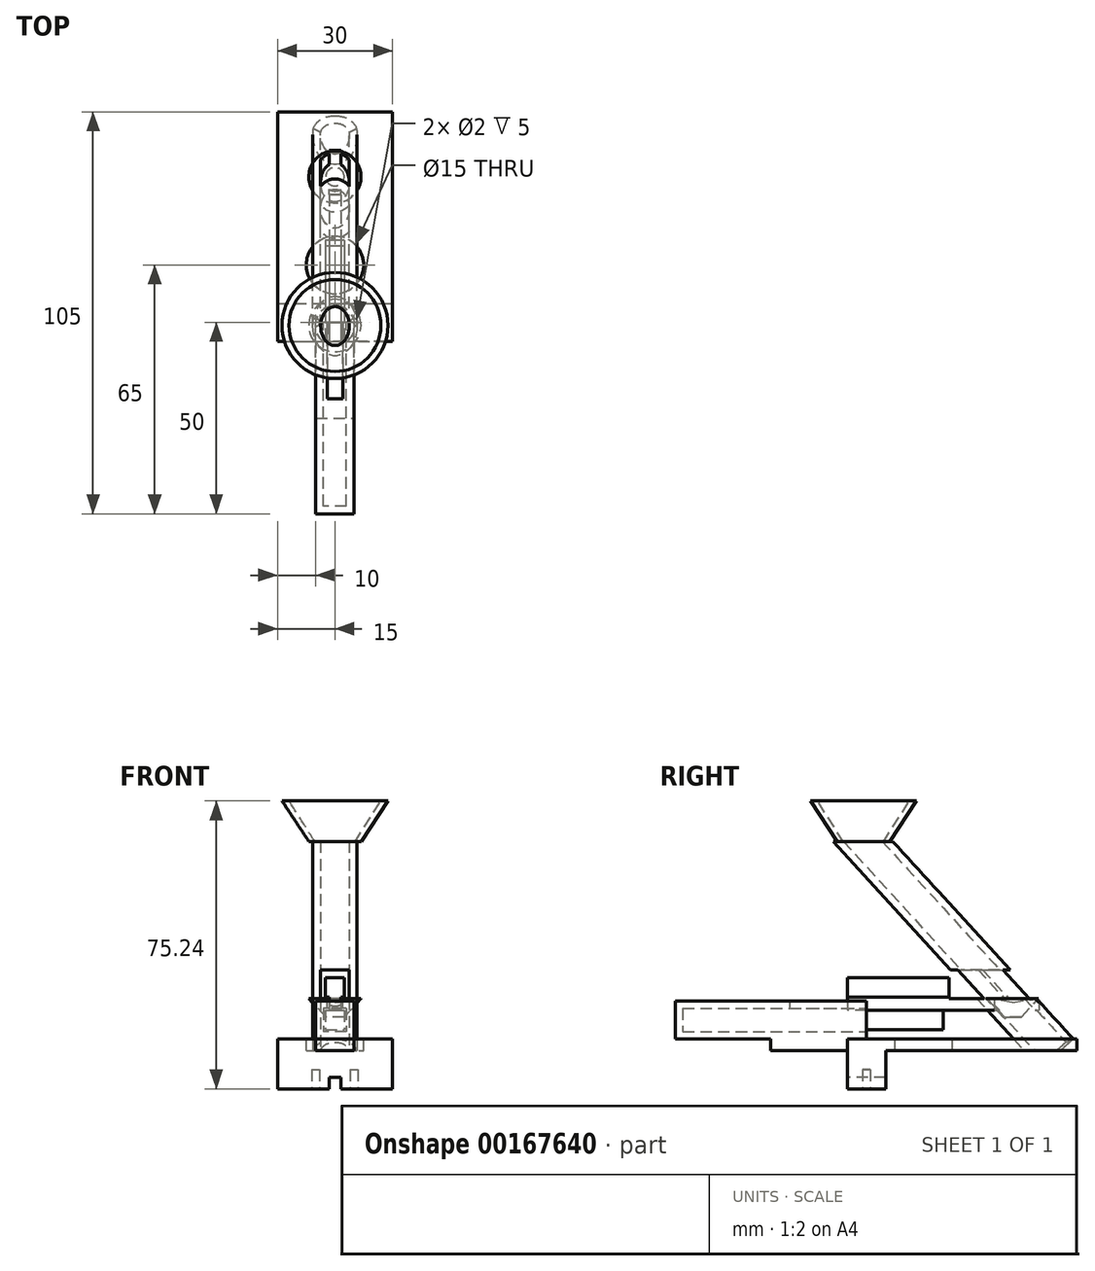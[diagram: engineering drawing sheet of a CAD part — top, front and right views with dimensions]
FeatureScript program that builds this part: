
annotation { "Feature Type Name" : "Feature", "Feature Type Description" : "" }
export const myFeature = defineFeature(function(context is Context, id is Id, definition is map)
    precondition{}
    {
        {
            var Q0;
            Q0=qCreatedBy(makeId("Front.planeOp"),FACE);
            var sketch = newSketch(context, id + "F0", { "sketchPlane" : qUnion([Q0])});
            skLineSegment(sketch, "E0.bottom", {"start": v(5, 5) * mm, "end": v(-5, 5) * mm});
            skLineSegment(sketch, "E0.top", {"start": v(5, -5) * mm, "end": v(-5, -5) * mm});
            skLineSegment(sketch, "E0.left", {"start": v(5, 5) * mm, "end": v(5, -5) * mm});
            skLineSegment(sketch, "E0.right", {"start": v(-5, 5) * mm, "end": v(-5, -5) * mm});
            skPoint(sketch, "E0.middle", {"position": v(0, 0) * mm});
            skLineSegment(sketch, "E1.bottom", {"start": v(3, 3) * mm, "end": v(-3, 3) * mm});
            skLineSegment(sketch, "E1.top", {"start": v(3, -3) * mm, "end": v(-3, -3) * mm});
            skLineSegment(sketch, "E1.left", {"start": v(3, 3) * mm, "end": v(3, -3) * mm});
            skLineSegment(sketch, "E1.right", {"start": v(-3, 3) * mm, "end": v(-3, -3) * mm});
            skSolve(sketch);
        }
        {
            var Q0;
            Q0=makeQuery(id+"F0.imprint","IMPRINT",FACE,{"disambiguationData":[TD([[makeQuery(id+"F0.imprint","IMPRINT",EDGE,{"derivedFrom":sQuery(id+"F0.wireOp",EDGE,"E0.bottom")}),1.0]])]});
            extrude(context, id + "F1", {"entities" : qUnion([Q0]), "depth" : 50 * mm});
        }
        {
            var Q0;
            {var subQ0=sQuery(id+"F0.wireOp",EDGE,"E0.bottom");Q0=makeQuery(id+"FmPY8GnlESxFqpJ_1.boolean.opBoolean","MERGE",FACE,{"derivedFrom":[makeQuery(id+"F1.opExtrude","SWEPT_FACE",FACE,{"disambiguationData":[OSD([subQ0])]}),makeQuery(id+"FmPY8GnlESxFqpJ_1.opExtrude","SWEPT_FACE",FACE,{"disambiguationData":[OSD([subQ0])]})]});}
            var sketch = newSketch(context, id + "F2", { "sketchPlane" : qUnion([Q0])});
            skLineSegment(sketch, "E2.bottom", {"start": v(-2, 0) * mm, "end": v(2, 0) * mm});
            skLineSegment(sketch, "E2.top", {"start": v(-2, -20) * mm, "end": v(2, -20) * mm});
            skLineSegment(sketch, "E2.left", {"start": v(-2, 0) * mm, "end": v(-2, -20) * mm});
            skLineSegment(sketch, "E2.right", {"start": v(2, 0) * mm, "end": v(2, -20) * mm});
            skSolve(sketch);
        }
        {
            var Q0;
            Q0=makeQuery(id+"F2.imprint","IMPRINT",FACE,{"disambiguationData":[TD([[makeQuery(id+"F2.imprint","IMPRINT",EDGE,{"derivedFrom":sQuery(id+"F2.wireOp",EDGE,"E2.bottom")}),1.0]])]});
            extrude(context, id + "F3", {"entities" : qUnion([Q0]), "operationType" : NewBodyOperationType.REMOVE, "oppositeDirection" : true, "depth" : 3 * mm});
        }
        {
            var Q0;
            Q0=makeQuery(id+"F1.opExtrude","CAP_FACE",FACE,{"disambiguationData":[OSD([sQuery(id+"F0.wireOp",EDGE,"E0.bottom"),sQuery(id+"F0.wireOp",EDGE,"E0.top"),sQuery(id+"F0.wireOp",EDGE,"E0.left"),sQuery(id+"F0.wireOp",EDGE,"E0.right"),sQuery(id+"F0.wireOp",EDGE,"E1.bottom"),sQuery(id+"F0.wireOp",EDGE,"E1.top"),sQuery(id+"F0.wireOp",EDGE,"E1.left"),sQuery(id+"F0.wireOp",EDGE,"E1.right")])],"isStart":true});
            var sketch = newSketch(context, id + "F4", { "sketchPlane" : qUnion([Q0])});
            skLineSegment(sketch, "E3.bottom", {"start": v(2.5, 2.5) * mm, "end": v(-2.5, 2.5) * mm});
            skLineSegment(sketch, "E3.top", {"start": v(2.5, -2.5) * mm, "end": v(-2.5, -2.5) * mm});
            skLineSegment(sketch, "E3.left", {"start": v(2.5, 2.5) * mm, "end": v(2.5, -2.5) * mm});
            skLineSegment(sketch, "E3.right", {"start": v(-2.5, 2.5) * mm, "end": v(-2.5, -2.5) * mm});
            skPoint(sketch, "E3.middle", {"position": v(0, 0) * mm});
            skSolve(sketch);
        }
        {
            var Q0;
            Q0=makeQuery(id+"F4.imprint","IMPRINT",FACE,{"disambiguationData":[TD([[makeQuery(id+"F4.imprint","IMPRINT",EDGE,{"derivedFrom":sQuery(id+"F4.wireOp",EDGE,"E3.bottom")}),1.0]])]});
            extrude(context, id + "F5", {"entities" : qUnion([Q0]), "depth" : 20 * mm});
        }
        {
            var Q0;
            Q0=makeQuery(id+"F5.opExtrude","CAP_FACE",FACE,{"disambiguationData":[OSD([sQuery(id+"F4.wireOp",EDGE,"E3.bottom"),sQuery(id+"F4.wireOp",EDGE,"E3.top"),sQuery(id+"F4.wireOp",EDGE,"E3.left"),sQuery(id+"F4.wireOp",EDGE,"E3.right")])],"isStart":false});
            var sketch = newSketch(context, id + "F6", { "sketchPlane" : qUnion([Q0])});
            skLineSegment(sketch, "E4.bottom", {"start": v(-2.5, 6) * mm, "end": v(-1.5, 6) * mm});
            skLineSegment(sketch, "E4.top", {"start": v(-2.5, 11) * mm, "end": v(2.5, 11) * mm});
            skLineSegment(sketch, "E4.left", {"start": v(-2.5, 6) * mm, "end": v(-2.5, 11) * mm});
            skLineSegment(sketch, "E4.right", {"start": v(2.5, 6) * mm, "end": v(2.5, 11) * mm});
            skPoint(sketch, "E4.middle", {"position": v(0, 8.5) * mm});
            skLineSegment(sketch, "E5", {"start": v(-1.5, 6) * mm, "end": v(-1.5, 2.5) * mm});
            skLineSegment(sketch, "E6", {"start": v(1.5, 6) * mm, "end": v(1.5, 2.5) * mm});
            skLineSegment(sketch, "E7.trimOffspring", {"start": v(1.5, 6) * mm, "end": v(2.5, 6) * mm});
            skSolve(sketch);
        }
        {
            var Q0;
            Q0=makeQuery(id+"F6.imprint","IMPRINT",FACE,{"disambiguationData":[TD([[makeQuery(id+"F6.imprint","IMPRINT",EDGE,{"derivedFrom":sQuery(id+"F6.wireOp",EDGE,"E4.bottom")}),1.0]])]});
            extrude(context, id + "F7", {"entities" : qUnion([Q0]), "operationType" : NewBodyOperationType.ADD, "depth" : 25 * mm, "hasSecondDirection" : true, "secondDirectionOppositeDirection" : true, "secondDirectionDepth" : 25 * mm});
        }
        {
            var Q0;
            {var subQ0=sQuery(id+"F0.wireOp",EDGE,"E0.top");Q0=makeQuery(id+"FmPY8GnlESxFqpJ_1.boolean.opBoolean","MERGE",FACE,{"derivedFrom":[makeQuery(id+"F1.opExtrude","SWEPT_FACE",FACE,{"disambiguationData":[OSD([subQ0])]}),makeQuery(id+"FmPY8GnlESxFqpJ_1.opExtrude","SWEPT_FACE",FACE,{"disambiguationData":[OSD([subQ0])]})]});}
            var sketch = newSketch(context, id + "F8", { "sketchPlane" : qUnion([Q0])});
            skPoint(sketch, "E8.firstSnap0", {"position": v(-5, 25) * mm});
            skLineSegment(sketch, "E8.bottom", {"start": v(-15, 25) * mm, "end": v(15, 25) * mm});
            skLineSegment(sketch, "E8.top", {"start": v(-15, -55) * mm, "end": v(15, -55) * mm});
            skLineSegment(sketch, "E8.left", {"start": v(-15, 25) * mm, "end": v(-15, -55) * mm});
            skLineSegment(sketch, "E8.right", {"start": v(15, 25) * mm, "end": v(15, -55) * mm});
            skSolve(sketch);
        }
        {
            var Q0;
            Q0 = qSketchRegion(id + "F8", true);
            extrude(context, id + "F9", {"entities" : qUnion([Q0]), "operationType" : NewBodyOperationType.ADD, "depth" : 3 * mm});
        }
        {
            var Q0;
            Q0=makeQuery(id+"F9.opExtrude","CAP_FACE",FACE,{"disambiguationData":[OSD([sQuery(id+"F8.wireOp",EDGE,"E8.bottom"),sQuery(id+"F8.wireOp",EDGE,"E8.top"),sQuery(id+"F8.wireOp",EDGE,"E8.left"),sQuery(id+"F8.wireOp",EDGE,"E8.right")])],"isStart":true});
            var sketch = newSketch(context, id + "F10", { "sketchPlane" : qUnion([Q0])});
            skCircle(sketch, "E9", {"center": v(0, 15) * mm, "radius": 7.5 * mm});
            skSolve(sketch);
        }
        {
            var Q0;
            Q0=makeQuery(id+"F10.imprint","IMPRINT",FACE,{"disambiguationData":[TD([[makeQuery(id+"F10.imprint","IMPRINT",EDGE,{"derivedFrom":sQuery(id+"F10.wireOp",EDGE,"E9")}),1.0]])]});
            extrude(context, id + "F11", {"entities" : qUnion([Q0]), "operationType" : NewBodyOperationType.REMOVE, "endBound" : BoundingType.THROUGH_ALL, "oppositeDirection" : true, "depth" : 25 * mm});
        }
        {
            var Q0;
            Q0=makeQuery(id+"F9.opExtrude","CAP_FACE",FACE,{"disambiguationData":[OSD([sQuery(id+"F8.wireOp",EDGE,"E8.bottom"),sQuery(id+"F8.wireOp",EDGE,"E8.top"),sQuery(id+"F8.wireOp",EDGE,"E8.left"),sQuery(id+"F8.wireOp",EDGE,"E8.right")])],"isStart":false});
            var sketch = newSketch(context, id + "F12", { "sketchPlane" : qUnion([Q0])});
            skLineSegment(sketch, "E10.bottom", {"start": v(-15, 5) * mm, "end": v(15, 5) * mm});
            skLineSegment(sketch, "E10.top", {"start": v(-15, -5) * mm, "end": v(15, -5) * mm});
            skLineSegment(sketch, "E10.left", {"start": v(-15, 5) * mm, "end": v(-15, -5) * mm});
            skLineSegment(sketch, "E10.right", {"start": v(15, 5) * mm, "end": v(15, -5) * mm});
            skSolve(sketch);
        }
        {
            var Q0;
            Q0=makeQuery(id+"F12.imprint","IMPRINT",FACE,{"disambiguationData":[TD([[makeQuery(id+"F12.imprint","IMPRINT",EDGE,{"derivedFrom":sQuery(id+"F12.wireOp",EDGE,"E10.bottom")}),-1.0]])]});
            extrude(context, id + "F13", {"entities" : qUnion([Q0]), "operationType" : NewBodyOperationType.ADD, "depth" : 10 * mm});
        }
        {
            var Q0;
            Q0=makeQuery(id+"F13.opExtrude","CAP_FACE",FACE,{"disambiguationData":[OSD([sQuery(id+"F12.wireOp",EDGE,"E10.bottom"),sQuery(id+"F12.wireOp",EDGE,"E10.top"),sQuery(id+"F12.wireOp",EDGE,"E10.left"),sQuery(id+"F12.wireOp",EDGE,"E10.right")])],"isStart":false});
            var sketch = newSketch(context, id + "F14", { "sketchPlane" : qUnion([Q0])});
            skLineSegment(sketch, "E11.bottom", {"start": v(1.5, -5) * mm, "end": v(-1.5, -5) * mm});
            skLineSegment(sketch, "E11.top", {"start": v(1.5, 5) * mm, "end": v(-1.5, 5) * mm});
            skLineSegment(sketch, "E11.left", {"start": v(1.5, -5) * mm, "end": v(1.5, 5) * mm});
            skLineSegment(sketch, "E11.right", {"start": v(-1.5, -5) * mm, "end": v(-1.5, 5) * mm});
            skSolve(sketch);
        }
        {
            var Q0;
            Q0=makeQuery(id+"F14.imprint","IMPRINT",FACE,{"disambiguationData":[TD([[makeQuery(id+"F14.imprint","IMPRINT",EDGE,{"derivedFrom":sQuery(id+"F14.wireOp",EDGE,"E11.bottom")}),1.0]])]});
            extrude(context, id + "F15", {"entities" : qUnion([Q0]), "operationType" : NewBodyOperationType.REMOVE, "oppositeDirection" : true, "depth" : 3 * mm});
        }
        {
            var Q0;
            {var subQ0=sQuery(id+"F12.wireOp",EDGE,"E10.left");var subQ1=sQuery(id+"F12.wireOp",EDGE,"E10.bottom");var subQ2=sQuery(id+"F12.wireOp",EDGE,"E10.top");Q0=makeQuery(id+"F15.boolean.opBoolean","SPLIT",FACE,{"disambiguationData":[TD([makeQuery(id+"F9.opExtrude","SWEPT_FACE",FACE,{"disambiguationData":[OSD([sQuery(id+"F8.wireOp",EDGE,"E8.left")])]})])],"derivedFrom":makeQuery(id+"F13.opExtrude","CAP_FACE",FACE,{"disambiguationData":[OSD([subQ1,subQ2,subQ0,sQuery(id+"F12.wireOp",EDGE,"E10.right")])],"isStart":false})});}
            var sketch = newSketch(context, id + "F16", { "sketchPlane" : qUnion([Q0])});
            skCircle(sketch, "E12", {"center": v(-5, 0) * mm, "radius": 1 * mm});
            skCircle(sketch, "E13", {"center": v(5, 0) * mm, "radius": 1 * mm});
            skSolve(sketch);
        }
        {
            var Q0;
            Q0 = qSketchRegion(id + "F16", true);
            extrude(context, id + "F17", {"entities" : qUnion([Q0]), "operationType" : NewBodyOperationType.REMOVE, "oppositeDirection" : true, "depth" : 5 * mm});
        }
        {
            var Q0;
            Q0=makeQuery(id+"F1.opExtrude","CAP_FACE",FACE,{"disambiguationData":[OSD([sQuery(id+"F0.wireOp",EDGE,"E0.bottom"),sQuery(id+"F0.wireOp",EDGE,"E0.top"),sQuery(id+"F0.wireOp",EDGE,"E0.left"),sQuery(id+"F0.wireOp",EDGE,"E0.right"),sQuery(id+"F0.wireOp",EDGE,"E1.bottom"),sQuery(id+"F0.wireOp",EDGE,"E1.top"),sQuery(id+"F0.wireOp",EDGE,"E1.left"),sQuery(id+"F0.wireOp",EDGE,"E1.right")])],"isStart":false});
            var sketch = newSketch(context, id + "F18", { "sketchPlane" : qUnion([Q0])});
            skLineSegment(sketch, "E14.bottom", {"start": v(-5, 5) * mm, "end": v(5, 5) * mm});
            skLineSegment(sketch, "E14.top", {"start": v(-5, -5) * mm, "end": v(5, -5) * mm});
            skLineSegment(sketch, "E14.left", {"start": v(-5, 5) * mm, "end": v(-5, -5) * mm});
            skLineSegment(sketch, "E14.right", {"start": v(5, 5) * mm, "end": v(5, -5) * mm});
            skSolve(sketch);
        }
        {
            var Q0;
            Q0=makeQuery(id+"F18.imprint","IMPRINT",FACE,{"disambiguationData":[TD([[makeQuery(id+"F18.imprint","IMPRINT",EDGE,{"derivedFrom":makeQuery(id+"F1.opExtrude","CAP_EDGE",EDGE,{"disambiguationData":[OSD([sQuery(id+"F0.wireOp",EDGE,"E1.bottom")])],"isStart":false})}),1.0]])]});
            extrude(context, id + "F19", {"entities" : qUnion([Q0]), "operationType" : NewBodyOperationType.ADD, "oppositeDirection" : true, "depth" : 2 * mm});
        }
        {
            var Q0;
            Q0=makeQuery(id+"F9.opExtrude","CAP_FACE",FACE,{"disambiguationData":[OSD([sQuery(id+"F8.wireOp",EDGE,"E8.bottom"),sQuery(id+"F8.wireOp",EDGE,"E8.top"),sQuery(id+"F8.wireOp",EDGE,"E8.left"),sQuery(id+"F8.wireOp",EDGE,"E8.right")])],"isStart":true});
            var sketch = newSketch(context, id + "F20", { "sketchPlane" : qUnion([Q0])});
            skLineSegment(sketch, "E15.bottom", {"start": v(-15, -25) * mm, "end": v(-5, -25) * mm});
            skLineSegment(sketch, "E15.top", {"start": v(-15, -5) * mm, "end": v(-5, -5) * mm});
            skLineSegment(sketch, "E15.left", {"start": v(-15, -25) * mm, "end": v(-15, -5) * mm});
            skLineSegment(sketch, "E15.right", {"start": v(-5, -25) * mm, "end": v(-5, -5) * mm});
            skLineSegment(sketch, "E16.bottom", {"start": v(15, -25) * mm, "end": v(5, -25) * mm});
            skLineSegment(sketch, "E16.top", {"start": v(15, -5) * mm, "end": v(5, -5) * mm});
            skLineSegment(sketch, "E16.left", {"start": v(15, -25) * mm, "end": v(15, -5) * mm});
            skLineSegment(sketch, "E16.right", {"start": v(5, -25) * mm, "end": v(5, -5) * mm});
            skSolve(sketch);
        }
        {
            var Q0;
            Q0=makeQuery(id+"F20.imprint","IMPRINT",FACE,{"disambiguationData":[TD([[makeQuery(id+"F20.imprint","IMPRINT",EDGE,{"derivedFrom":sQuery(id+"F20.wireOp",EDGE,"E15.bottom")}),1.0]])]});
            var Q1;
            Q1=makeQuery(id+"F20.imprint","IMPRINT",FACE,{"disambiguationData":[TD([[makeQuery(id+"F20.imprint","IMPRINT",EDGE,{"derivedFrom":sQuery(id+"F20.wireOp",EDGE,"E16.bottom")}),1.0]])]});
            extrude(context, id + "F21", {"entities" : qUnion([Q0, Q1]), "operationType" : NewBodyOperationType.REMOVE, "oppositeDirection" : true, "depth" : 25 * mm});
        }
        {
            var Q0;
            Q0=qCreatedBy(makeId("Right.planeOp"),FACE);
            var sketch = newSketch(context, id + "F22", { "sketchPlane" : qUnion([Q0])});
            skLineSegment(sketch, "E17", {"start": v(51.9, -11.16) * mm, "end": v(-6.02, 52.19) * mm, "construction": true});
            skLineSegment(sketch, "E18", {"start": v(52.08, -5.8) * mm, "end": v(-2.06, 53.41) * mm});
            skLineSegment(sketch, "E19", {"start": v(-2.06, 53.41) * mm, "end": v(-0.58, 54.76) * mm});
            skLineSegment(sketch, "E20", {"start": v(-0.58, 54.76) * mm, "end": v(54, -4.95) * mm});
            skLineSegment(sketch, "E21", {"start": v(54, -4.95) * mm, "end": v(52.08, -5.8) * mm});
            skSolve(sketch);
        }
        {
            var Q0;
            Q0=makeQuery(id+"F22.imprint","IMPRINT",FACE,{"disambiguationData":[TD([[makeQuery(id+"F22.imprint","IMPRINT",EDGE,{"derivedFrom":sQuery(id+"F22.wireOp",EDGE,"E18")}),-1.0]])]});
            var Q1;
            Q1=sQuery(id+"F22.wireOp",EDGE,"E17");
            revolve(context, id + "F23", {"entities" : qUnion([Q0]), "axis" : qUnion([Q1]), "revolveType" : RevolveType.FULL});
        }
        {
            var Q0;
            Q0=makeQuery(id+"F9.opExtrude","SWEPT_FACE",FACE,{"disambiguationData":[OSD([sQuery(id+"F8.wireOp",EDGE,"E8.top")])]});
            cPlane(context, id + "F24", {"entities" : qUnion([Q0]), "cplaneType" : CPlaneType.OFFSET, "offset" : 0 * mm, "width" : 150 * mm, "height" : 150 * mm});
        }
        {
            var Q0;
            Q0=qCreatedBy(id+"F24.planeOp",FACE);
            var sketch = newSketch(context, id + "F25", { "sketchPlane" : qUnion([Q0])});
            skLineSegment(sketch, "E22.bottom", {"start": v(-3.77, 13.1) * mm, "end": v(3.73, 13.1) * mm});
            skLineSegment(sketch, "E22.top", {"start": v(-3.77, 5.6) * mm, "end": v(3.73, 5.6) * mm});
            skLineSegment(sketch, "E22.left", {"start": v(-3.77, 13.1) * mm, "end": v(-3.77, 5.6) * mm});
            skLineSegment(sketch, "E22.right", {"start": v(3.73, 13.1) * mm, "end": v(3.73, 5.6) * mm});
            skSolve(sketch);
        }
        {
            var Q0;
            Q0=makeQuery(id+"F25.imprint","IMPRINT",FACE,{"disambiguationData":[TD([[makeQuery(id+"F25.imprint","IMPRINT",EDGE,{"derivedFrom":sQuery(id+"F25.wireOp",EDGE,"E22.bottom")}),-1.0]])]});
            extrude(context, id + "F26", {"entities" : qUnion([Q0]), "operationType" : NewBodyOperationType.REMOVE, "oppositeDirection" : true, "depth" : 33.5 * mm});
        }
        {
            var Q0;
            Q0=makeQuery(id+"F7.opExtrude","CAP_FACE",FACE,{"disambiguationData":[OSD([sQuery(id+"F4.wireOp",EDGE,"E3.bottom"),sQuery(id+"F6.wireOp",EDGE,"E4.bottom"),sQuery(id+"F6.wireOp",EDGE,"E4.top"),sQuery(id+"F6.wireOp",EDGE,"E4.left"),sQuery(id+"F6.wireOp",EDGE,"E4.right"),sQuery(id+"F6.wireOp",EDGE,"E5"),sQuery(id+"F6.wireOp",EDGE,"E6"),sQuery(id+"F6.wireOp",EDGE,"E7.trimOffspring")])],"isStart":false});
            var sketch = newSketch(context, id + "F27", { "sketchPlane" : qUnion([Q0])});
            skLineSegment(sketch, "E23.bottom", {"start": v(1.5, 2.5) * mm, "end": v(-1.5, 2.5) * mm});
            skLineSegment(sketch, "E23.top", {"start": v(1.5, 6) * mm, "end": v(-1.5, 6) * mm});
            skLineSegment(sketch, "E23.left", {"start": v(1.5, 2.5) * mm, "end": v(1.5, 6) * mm});
            skLineSegment(sketch, "E23.right", {"start": v(-1.5, 2.5) * mm, "end": v(-1.5, 6) * mm});
            skSolve(sketch);
        }
        {
            var Q0;
            Q0=makeQuery(id+"F27.imprint","IMPRINT",FACE,{"disambiguationData":[TD([[makeQuery(id+"F27.imprint","IMPRINT",EDGE,{"derivedFrom":sQuery(id+"F27.wireOp",EDGE,"E23.bottom")}),-1.0]])]});
            extrude(context, id + "F28", {"entities" : qUnion([Q0]), "operationType" : NewBodyOperationType.REMOVE, "oppositeDirection" : true, "depth" : 11.6 * mm});
        }
        {
            var Q0;
            Q0=qCreatedBy(makeId("Right.planeOp"),FACE);
            var sketch = newSketch(context, id + "F29", { "sketchPlane" : qUnion([Q0])});
            skLineSegment(sketch, "E24.bottom", {"start": v(-17.3, 46.63) * mm, "end": v(17.14, 46.63) * mm});
            skLineSegment(sketch, "E24.top", {"start": v(-17.3, 64.16) * mm, "end": v(17.14, 64.16) * mm});
            skLineSegment(sketch, "E24.left", {"start": v(-17.3, 46.63) * mm, "end": v(-17.3, 64.16) * mm});
            skLineSegment(sketch, "E24.right", {"start": v(17.14, 46.63) * mm, "end": v(17.14, 64.16) * mm});
            skSolve(sketch);
        }
        {
            var Q0;
            Q0=makeQuery(id+"F29.imprint","IMPRINT",FACE,{"disambiguationData":[TD([[makeQuery(id+"F29.imprint","IMPRINT",EDGE,{"derivedFrom":sQuery(id+"F29.wireOp",EDGE,"E24.bottom")}),1.0]])]});
            extrude(context, id + "F30", {"entities" : qUnion([Q0]), "operationType" : NewBodyOperationType.REMOVE, "endBound" : BoundingType.SYMMETRIC, "oppositeDirection" : true, "depth" : 1210 * mm});
        }
        {
            var Q0;
            Q0=qCreatedBy(makeId("Right.planeOp"),FACE);
            var sketch = newSketch(context, id + "F31", { "sketchPlane" : qUnion([Q0])});
            skLineSegment(sketch, "E25", {"start": v(4.38, 46.47) * mm, "end": v(11.2, 57.24) * mm});
            skLineSegment(sketch, "E26", {"start": v(11.2, 57.24) * mm, "end": v(13.04, 57.24) * mm});
            skLineSegment(sketch, "E27", {"start": v(13.04, 57.24) * mm, "end": v(6.02, 46.65) * mm});
            skLineSegment(sketch, "E28", {"start": v(6.02, 46.65) * mm, "end": v(4.38, 46.47) * mm});
            skLineSegment(sketch, "E29", {"start": v(-0.8, 46.64) * mm, "end": v(-0.8, 57.8) * mm, "construction": true});
            skSolve(sketch);
        }
        {
            var Q0;
            Q0=makeQuery(id+"F31.imprint","IMPRINT",FACE,{"disambiguationData":[TD([[makeQuery(id+"F31.imprint","IMPRINT",EDGE,{"derivedFrom":sQuery(id+"F31.wireOp",EDGE,"E25")}),-1.0]])]});
            var Q1;
            Q1=sQuery(id+"F31.wireOp",EDGE,"E29");
            revolve(context, id + "F32", {"entities" : qUnion([Q0]), "axis" : qUnion([Q1]), "revolveType" : RevolveType.FULL});
        }
        {
            var Q0;
            Q0=makeQuery(id+"F13.boolean.opBoolean","MERGE",FACE,{"derivedFrom":[makeQuery(id+"F9.opExtrude","SWEPT_FACE",FACE,{"disambiguationData":[OSD([sQuery(id+"F8.wireOp",EDGE,"E8.right")])]}),makeQuery(id+"F13.opExtrude","SWEPT_FACE",FACE,{"disambiguationData":[OSD([sQuery(id+"F12.wireOp",EDGE,"E10.right")])]})]});
            var sketch = newSketch(context, id + "F33", { "sketchPlane" : qUnion([Q0])});
            skLineSegment(sketch, "E30.bottom", {"start": v(55, -8) * mm, "end": v(38.5, -8) * mm});
            skLineSegment(sketch, "E30.top", {"start": v(55, -13.46) * mm, "end": v(38.5, -13.46) * mm});
            skLineSegment(sketch, "E30.left", {"start": v(55, -8) * mm, "end": v(55, -13.46) * mm});
            skLineSegment(sketch, "E30.right", {"start": v(38.5, -8) * mm, "end": v(38.5, -13.46) * mm});
            skSolve(sketch);
        }
        {
            var Q0;
            Q0 = qSketchRegion(id + "F33", true);
            extrude(context, id + "F34", {"entities" : qUnion([Q0]), "operationType" : NewBodyOperationType.REMOVE, "oppositeDirection" : true, "depth" : 25 * mm});
        }
        {
            var Q0;
            Q0=qCreatedBy(makeId("Right.planeOp"),FACE);
            var sketch = newSketch(context, id + "F35", { "sketchPlane" : qUnion([Q0])});
            skLineSegment(sketch, "E31", {"start": v(35.63, 0.78) * mm, "end": v(31.24, 5.57) * mm});
            skLineSegment(sketch, "E32", {"start": v(31.24, 5.57) * mm, "end": v(38.06, 4.59) * mm});
            skLineSegment(sketch, "E33", {"start": v(35.63, 0.78) * mm, "end": v(38.06, 0.78) * mm});
            skLineSegment(sketch, "E34", {"start": v(38.06, 4.59) * mm, "end": v(38.06, 0.78) * mm});
            skSolve(sketch);
        }
        {
            var Q0;
            Q0=makeQuery(id+"F35.imprint","IMPRINT",FACE,{"disambiguationData":[TD([[makeQuery(id+"F35.imprint","IMPRINT",EDGE,{"derivedFrom":sQuery(id+"F35.wireOp",EDGE,"E31")}),-1.0]])]});
            var Q1;
            Q1=sQuery(id+"F35.wireOp",EDGE,"E34");
            revolve(context, id + "F36", {"entities" : qUnion([Q0]), "axis" : qUnion([Q1]), "revolveType" : RevolveType.FULL});
        }
    });
